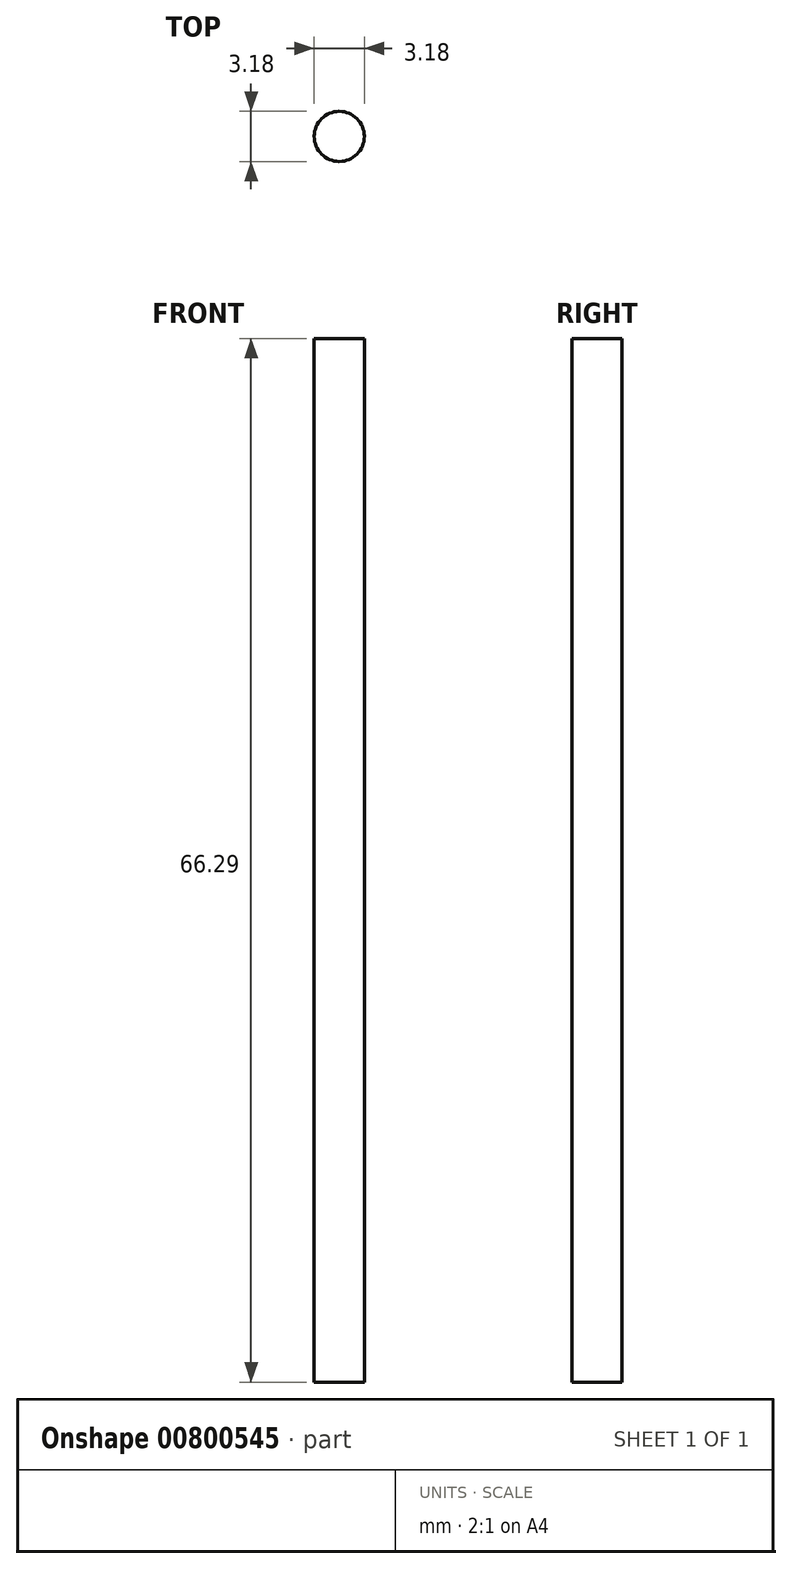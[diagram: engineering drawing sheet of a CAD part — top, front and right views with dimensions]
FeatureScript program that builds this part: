
annotation { "Feature Type Name" : "Feature", "Feature Type Description" : "" }
export const myFeature = defineFeature(function(context is Context, id is Id, definition is map)
    precondition{}
    {
        {
            var Q0;
            Q0=qCreatedBy(makeId("Top.planeOp"),FACE);
            var sketch = newSketch(context, id + "F0", { "sketchPlane" : qUnion([Q0])});
            skCircle(sketch, "E0", {"center": v(0, 0) * mm, "radius": 1.6 * mm});
            skSolve(sketch);
        }
        {
            var Q0;
            Q0=makeQuery(id+"F0.imprint","IMPRINT",FACE,{"disambiguationData":[TD([[makeQuery(id+"F0.imprint","IMPRINT",EDGE,{"derivedFrom":sQuery(id+"F0.wireOp",EDGE,"E0")}),1.0]])]});
            extrude(context, id + "F1", {"entities" : qUnion([Q0]), "depth" : 66.3 * mm, "offsetDistance" : 25.4 * mm});
        }
    });
